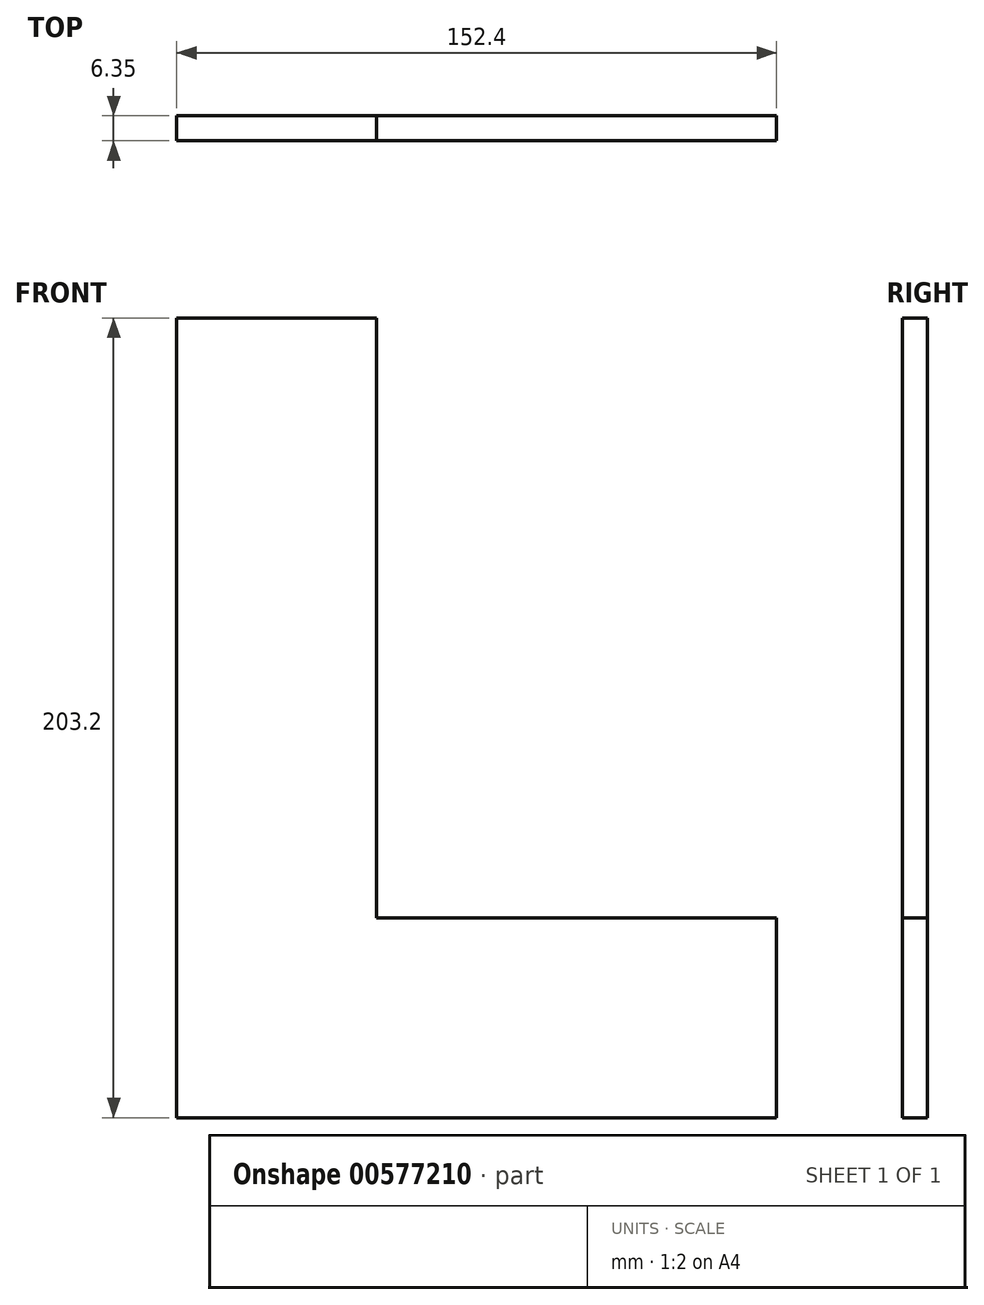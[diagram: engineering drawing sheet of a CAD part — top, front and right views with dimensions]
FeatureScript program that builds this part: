
annotation { "Feature Type Name" : "Feature", "Feature Type Description" : "" }
export const myFeature = defineFeature(function(context is Context, id is Id, definition is map)
    precondition{}
    {
        {
            var Q0;
            Q0=qCreatedBy(makeId("Front.planeOp"),FACE);
            var sketch = newSketch(context, id + "F0", { "sketchPlane" : qUnion([Q0])});
            skLineSegment(sketch, "E0", {"start": v(0, 0) * mm, "end": v(0, 203.2) * mm});
            skLineSegment(sketch, "E1", {"start": v(0, 203.2) * mm, "end": v(50.8, 203.2) * mm});
            skLineSegment(sketch, "E2", {"start": v(50.8, 203.2) * mm, "end": v(50.8, 50.8) * mm});
            skLineSegment(sketch, "E3", {"start": v(50.8, 50.8) * mm, "end": v(152.4, 50.8) * mm});
            skLineSegment(sketch, "E4", {"start": v(152.4, 50.8) * mm, "end": v(152.4, 0) * mm});
            skLineSegment(sketch, "E5", {"start": v(152.4, 0) * mm, "end": v(0, 0) * mm});
            skSolve(sketch);
        }
        {
            var Q0;
            Q0=makeQuery(id+"F0.imprint","IMPRINT",FACE,{"disambiguationData":[TD([[makeQuery(id+"F0.imprint","IMPRINT",EDGE,{"derivedFrom":sQuery(id+"F0.wireOp",EDGE,"E0")}),-1.0]])]});
            extrude(context, id + "F1", {"entities" : qUnion([Q0]), "depth" : 6.35 * mm, "offsetDistance" : 25.4 * mm});
        }
    });
